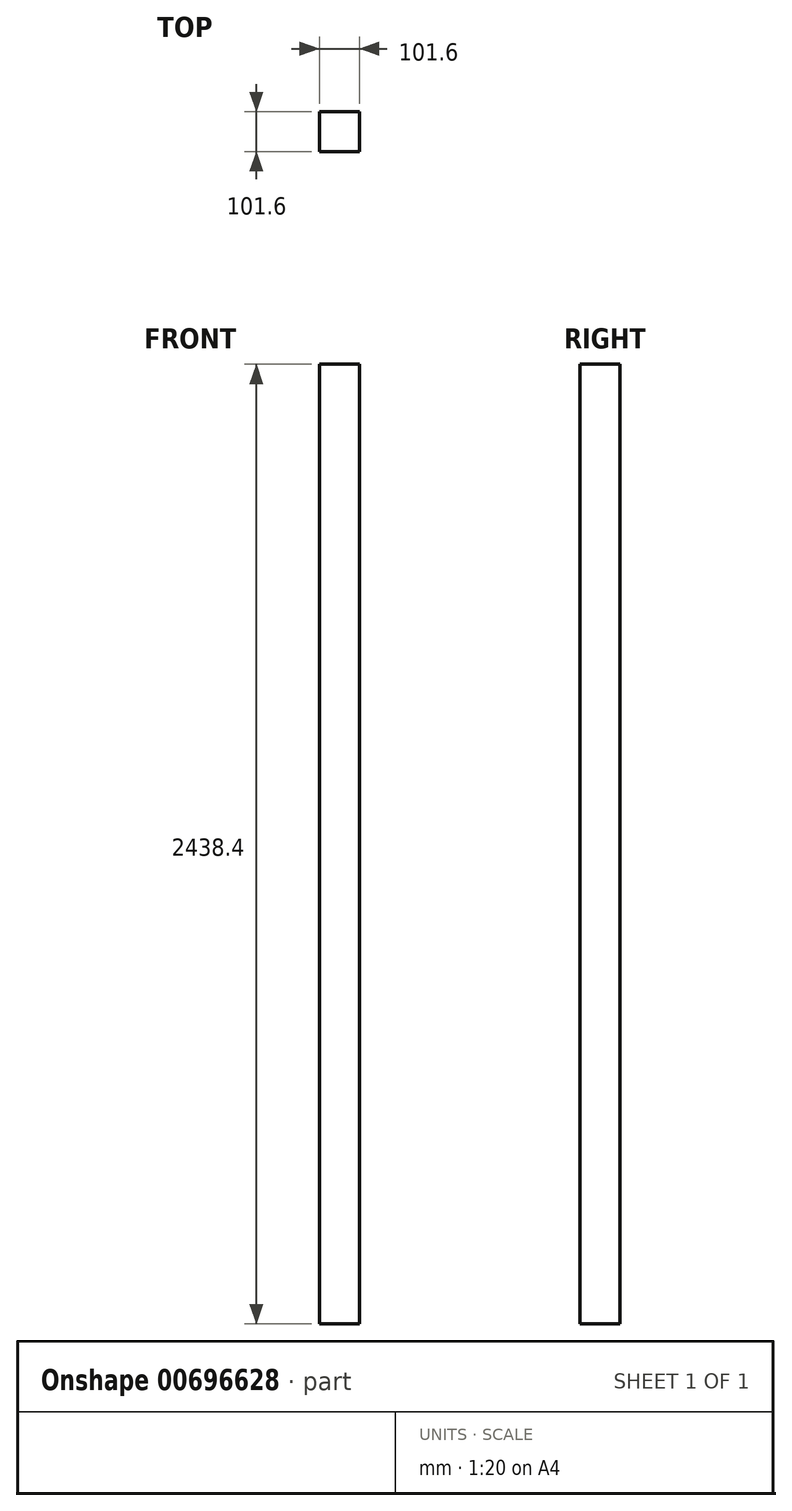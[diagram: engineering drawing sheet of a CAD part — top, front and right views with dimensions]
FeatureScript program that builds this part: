
annotation { "Feature Type Name" : "Feature", "Feature Type Description" : "" }
export const myFeature = defineFeature(function(context is Context, id is Id, definition is map)
    precondition{}
    {
        {
            var Q0;
            Q0=qCreatedBy(makeId("Top.planeOp"),FACE);
            var sketch = newSketch(context, id + "F0", { "sketchPlane" : qUnion([Q0])});
            skLineSegment(sketch, "E0.bottom", {"start": v(50.8, -50.8) * mm, "end": v(-50.8, -50.8) * mm});
            skLineSegment(sketch, "E0.top", {"start": v(50.8, 50.8) * mm, "end": v(-50.8, 50.8) * mm});
            skLineSegment(sketch, "E0.left", {"start": v(50.8, -50.8) * mm, "end": v(50.8, 50.8) * mm});
            skLineSegment(sketch, "E0.right", {"start": v(-50.8, -50.8) * mm, "end": v(-50.8, 50.8) * mm});
            skPoint(sketch, "E0.middle", {"position": v(0, 0) * mm});
            skSolve(sketch);
        }
        {
            var Q0;
            Q0=makeQuery(id+"F0.imprint","IMPRINT",FACE,{"disambiguationData":[TD([[makeQuery(id+"F0.imprint","IMPRINT",EDGE,{"derivedFrom":sQuery(id+"F0.wireOp",EDGE,"E0.bottom")}),-1.0]])]});
            extrude(context, id + "F1", {"entities" : qUnion([Q0]), "depth" : 2438.4 * mm, "offsetDistance" : 25.4 * mm});
        }
    });
